# Revit family: rba-bim-rba4110-940
name_source: partatom
category: Plumbing Fixtures
revit_build: Autodesk Revit 2018 (Build: 20170223_1515(x64)
units: mm (PartAtom-declared; Revit-internal decimal feet)

## family parameters
Always vertical = Yes
Cut with Voids When Loaded = No
Part Type = Normal
Room Calculation Point = No
Round Connector Dimension = Use Diameter
Shared = Yes
Work Plane-Based = No

## types (1)
- RBA4110-940
    CW Connection = Yes
    Description = Handset, Hose & Slider
    Distance Away from Toilet (default) = 1090 mm  [stored 3.57612 ft]
    Distance Away from Wall (default) = 100 mm  [stored 0.328084 ft]
    HW Connection = Yes
    Manufacturer = RBA Group
    Materials and Finishes = Stainless Steel AISI 304
    Model = RBA4110-940
    Modified Issue = 20190529.01
    OFFSET = 1000 mm  [stored 3.28084 ft]
    URL = www.rba.com.au
    Vent Connection = Yes
    Waste Connection = Yes

note: [stored X ft] marks values corroborated as IEEE doubles in the binary element streams (Revit-internal decimal feet)

## geometry (parser evidence)
native form markers: Blend x2, Sweep x3
no freeform markers — native parametric forms only
